# Revit family: Valve-Thermostatic-Waterworks-Universal
name_source: partatom
category: Pipe Accessories
revit_build: Autodesk Revit MEP 2014 (Build: 20140709_2115(x64)
units: mm (PartAtom-declared; Revit-internal decimal feet)

## types (1)
- Universal 1/2" Thermostatic Valve
    Anti-scald Protection = Yes
    Assembly Code = D2010
    Certification CSA = Yes
    Certification IAPMO = Yes
    Certification State of MA = Yes
    Certification UPC = Yes
    Certification cUPC = Yes
    Code Compliance = Code # GUSV56: Certified with cUPC, NSF, IAPMO, CSA
    Cold Water Inlet Connection = Inlet - Female NPT
    Cold Water Inlet Diameter = 0' - 0 1/2"
    Depth = 0' - 5 1/2"
    Description = Universal 1/2” Thermostatic Valve
    Finish = Metal - Waterworks - Unfinished
    Fittings Hole Diameter = 0' - 4 1/2"
    Height = 0' - 2 3/4"
    Hot Water Inlet Connection = Inlet - Female NPT
    Hot Water Inlet Diameter = 0' - 0 1/2"
    Keynote = 22 40 00
    Length = 0' - 7"
    Manufacturer = Waterworks
    Mixed Water Bottom Outlet Diameter = 0' - 0 1/2"
    Mixed Water Outlet Bottom Connection = Outlet - Female NPT
    Mixed Water Outlet Top Connection = Outlet - Female NPT
    Mixed Water Top Outlet Diameter = 0' - 0 1/2"
    Model = GUTH56
    Model SKU = 26-80190-84003
    Pressure = 45.00 psi
    Product Documentation Link = http://assets.waterworks.com
    Product Name = Universal 1/2” Thermostatic Valve
    Product Page URL = http://www.waterworks.com
    URL = http://www.waterworks.com
    Version = 2014 - v1.0a
    Warranty = http://www.waterworks.com
    Water Pressure = Max: 85psi / Min: 20psi / Recommended: 45psi
    ‌Installation Requirements or Notes = This valve features anti-scald protection. The risk of scalding exists until the installer has properly calibrated/adjusted the temperature setting prior to final trim installation.

## geometry (parser evidence)
native form markers: Sweep x1
no freeform markers — native parametric forms only
